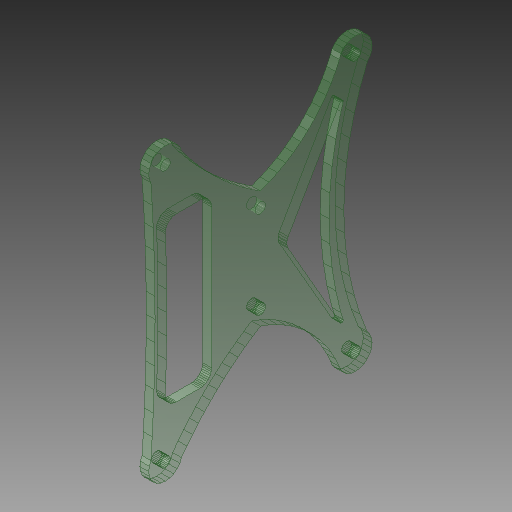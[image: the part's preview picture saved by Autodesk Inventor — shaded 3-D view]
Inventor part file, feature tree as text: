
AUTODESK INVENTOR PART (.ipt)
format: ipt  version: 2017 (Build 210142000, 142)  size: 567,296 bytes
history: native  units: mm
features: extrude x3, sketch x3
ambient origin geometry x8: Origin, YZ Plane, XZ Plane, XY Plane, X Axis, Y Axis, Z Axis, Center Point
bodies: Solid1 (feature_tree)
feature tree (6):
  extrude  "Extrusion1"  Depth=3.0mm
  extrude  "Extrusion2"  Depth=3.0mm
  extrude  "Extrusion3"  [1 undecoded]
  sketch  "Sketch1"  dims[d0=3.0mm d1=0.0mm d2=3.4mm]
  sketch  "Sketch2"  dims[d3=3.0mm d4=0.0mm d5=3.5mm]
  sketch  "Sketch3"  dims[d6=10.0mm d7=0.0mm]
note: 1 required parameter value undecoded (feature->parameter linkage not recoverable at this tier; creation-order binding heuristic only, values carry confidence <= 0.55)
